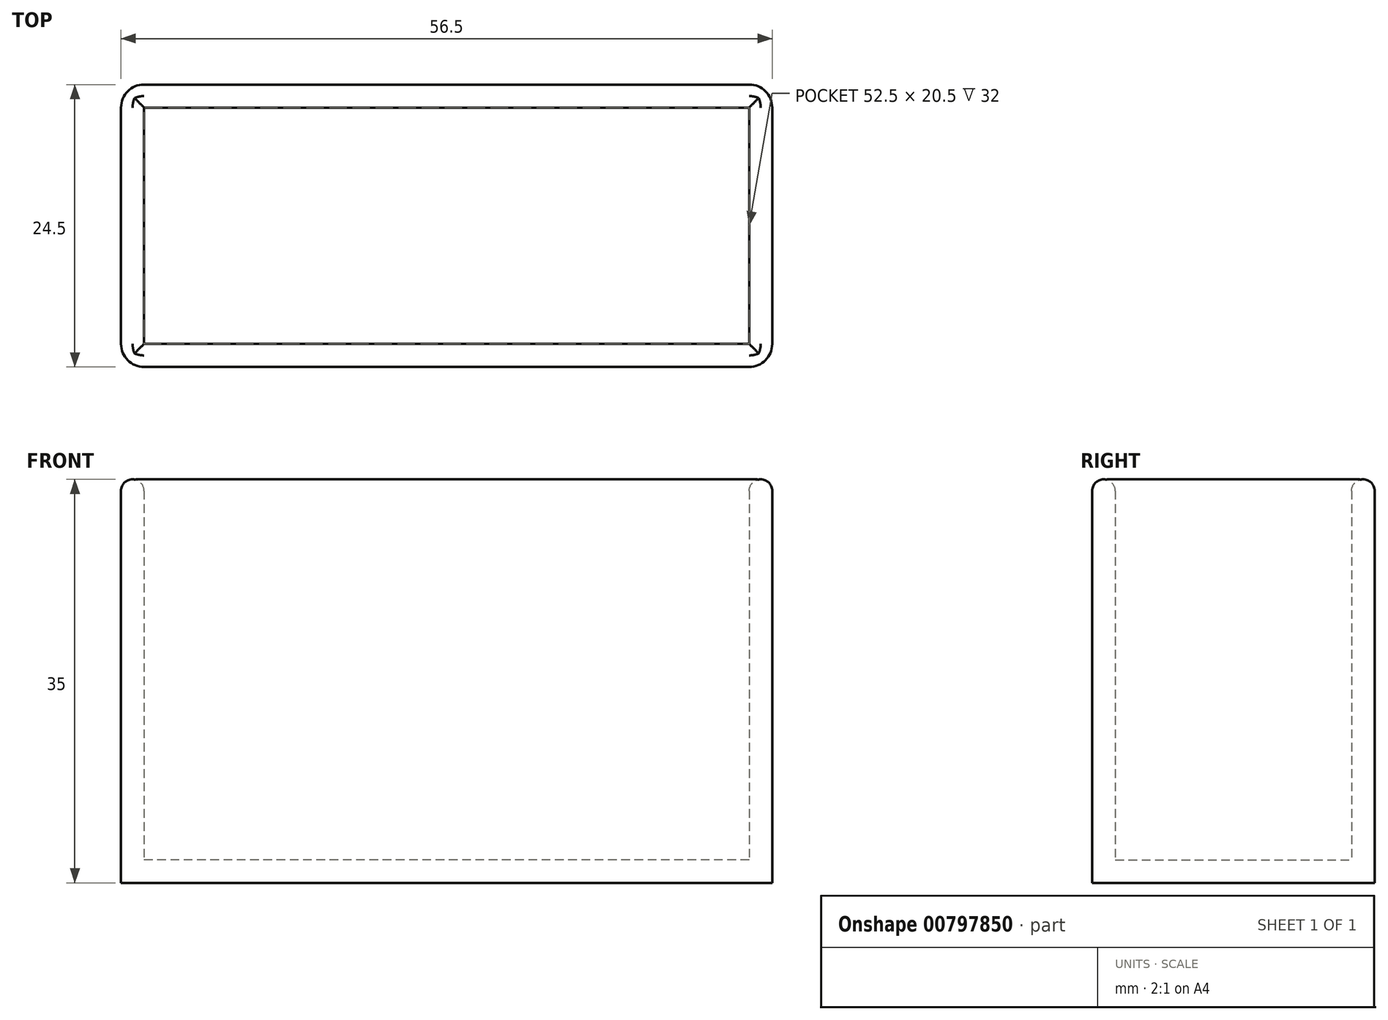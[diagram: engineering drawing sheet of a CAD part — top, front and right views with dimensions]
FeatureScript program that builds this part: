
annotation { "Feature Type Name" : "Feature", "Feature Type Description" : "" }
export const myFeature = defineFeature(function(context is Context, id is Id, definition is map)
    precondition{}
    {
        {
            var Q0;
            Q0=qCreatedBy(makeId("Top.planeOp"),FACE);
            var sketch = newSketch(context, id + "F0", { "sketchPlane" : qUnion([Q0])});
            skPoint(sketch, "E0.middle", {"position": v(0, 0) * mm});
            skLineSegment(sketch, "E1.bottom", {"start": v(28.25, -12.25) * mm, "end": v(-28.25, -12.25) * mm});
            skLineSegment(sketch, "E1.top", {"start": v(28.25, 12.25) * mm, "end": v(-28.25, 12.25) * mm});
            skLineSegment(sketch, "E1.left", {"start": v(28.25, -12.25) * mm, "end": v(28.25, 12.25) * mm});
            skLineSegment(sketch, "E1.right", {"start": v(-28.25, -12.25) * mm, "end": v(-28.25, 12.25) * mm});
            skSolve(sketch);
        }
        {
            var Q0;
            Q0=makeQuery(id+"F0.imprint","IMPRINT",FACE,{"disambiguationData":[TD([[makeQuery(id+"F0.imprint","IMPRINT",EDGE,{"derivedFrom":sQuery(id+"F0.wireOp",EDGE,"E1.bottom")}),-1.0]])]});
            extrude(context, id + "F1", {"entities" : qUnion([Q0]), "depth" : 35 * mm, "offsetDistance" : 25 * mm});
        }
        {
            var Q0;
            Q0=makeQuery(id+"F1.opExtrude","CAP_FACE",FACE,{"disambiguationData":[OSD([sQuery(id+"F0.wireOp",EDGE,"E1.bottom"),sQuery(id+"F0.wireOp",EDGE,"E1.top"),sQuery(id+"F0.wireOp",EDGE,"E1.left"),sQuery(id+"F0.wireOp",EDGE,"E1.right")])],"isStart":false});
            shell(context, id + "F2", {"entities" : qUnion([Q0]), "thickness" : 2 * mm});
        }
        {
            var Q0;
            Q0=makeQuery(id+"F1.opExtrude","SWEPT_EDGE",EDGE,{"disambiguationData":[OSD([sQuery(id+"F0.wireOp",EDGE,"E1.bottom"),sQuery(id+"F0.wireOp",EDGE,"E1.right")])]});
            var Q1;
            Q1=makeQuery(id+"F1.opExtrude","SWEPT_EDGE",EDGE,{"disambiguationData":[OSD([sQuery(id+"F0.wireOp",EDGE,"E1.top"),sQuery(id+"F0.wireOp",EDGE,"E1.right")])]});
            var Q2;
            Q2=makeQuery(id+"F1.opExtrude","SWEPT_EDGE",EDGE,{"disambiguationData":[OSD([sQuery(id+"F0.wireOp",EDGE,"E1.bottom"),sQuery(id+"F0.wireOp",EDGE,"E1.left")])]});
            var Q3;
            Q3=makeQuery(id+"F1.opExtrude","SWEPT_EDGE",EDGE,{"disambiguationData":[OSD([sQuery(id+"F0.wireOp",EDGE,"E1.top"),sQuery(id+"F0.wireOp",EDGE,"E1.left")])]});
            fillet(context, id + "F3", {"entities" : qUnion([Q0, Q1, Q2, Q3]), "radius" : 2 * mm, "tangentPropagation" : true, "allowEdgeOverflow" : false});
        }
        {
            var Q0;
            {var subQ0=sQuery(id+"F0.wireOp",EDGE,"E1.bottom");Q0=makeQuery(id+"F2.opShell","OFFSET_EDGE",EDGE,{"disambiguationData":[OSD([subQ0]),TDD([makeQuery(id+"F1.opExtrude","CAP_EDGE",EDGE,{"disambiguationData":[OSD([subQ0])],"isStart":false})])]});}
            var Q1;
            {var subQ0=sQuery(id+"F0.wireOp",EDGE,"E1.right");Q1=makeQuery(id+"F2.opShell","OFFSET_EDGE",EDGE,{"disambiguationData":[OSD([subQ0]),TDD([makeQuery(id+"F1.opExtrude","CAP_EDGE",EDGE,{"disambiguationData":[OSD([subQ0])],"isStart":false})])]});}
            var Q2;
            {var subQ0=sQuery(id+"F0.wireOp",EDGE,"E1.top");Q2=makeQuery(id+"F2.opShell","OFFSET_EDGE",EDGE,{"disambiguationData":[OSD([subQ0]),TDD([makeQuery(id+"F1.opExtrude","CAP_EDGE",EDGE,{"disambiguationData":[OSD([subQ0])],"isStart":false})])]});}
            var Q3;
            {var subQ0=sQuery(id+"F0.wireOp",EDGE,"E1.left");Q3=makeQuery(id+"F2.opShell","OFFSET_EDGE",EDGE,{"disambiguationData":[OSD([subQ0]),TDD([makeQuery(id+"F1.opExtrude","CAP_EDGE",EDGE,{"disambiguationData":[OSD([subQ0])],"isStart":false})])]});}
            fillet(context, id + "F4", {"entities" : qUnion([Q0, Q1, Q2, Q3]), "radius" : 1 * mm, "tangentPropagation" : true, "allowEdgeOverflow" : false});
        }
        {
            var Q0;
            Q0=makeQuery(id+"F1.opExtrude","CAP_EDGE",EDGE,{"disambiguationData":[OSD([sQuery(id+"F0.wireOp",EDGE,"E1.bottom")])],"isStart":false});
            fillet(context, id + "F5", {"entities" : qUnion([Q0]), "radius" : 1 * mm, "tangentPropagation" : true, "allowEdgeOverflow" : false});
        }
    });
